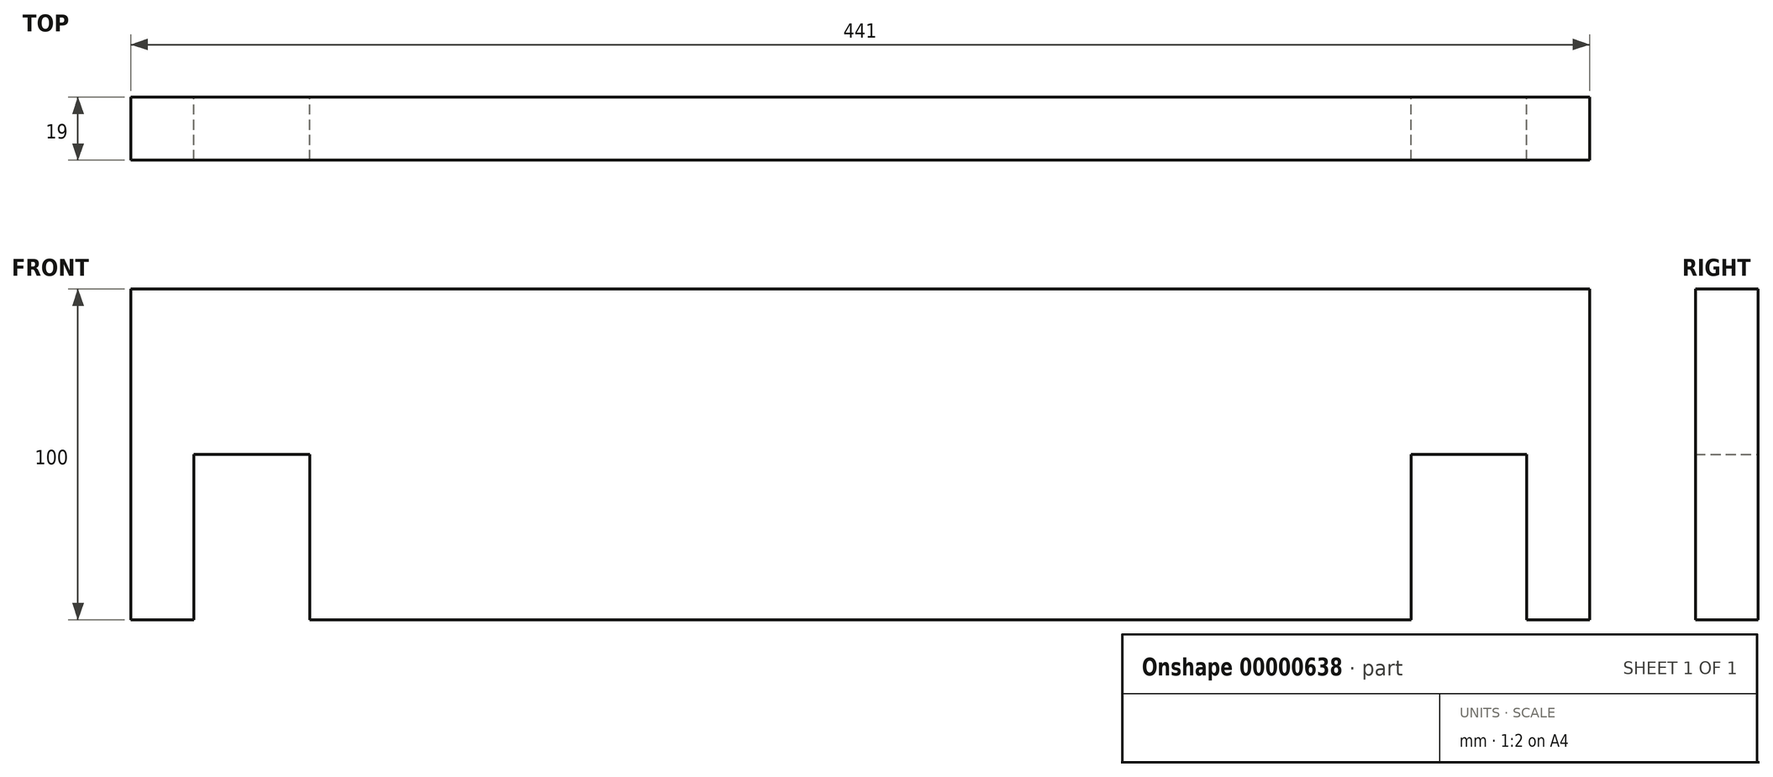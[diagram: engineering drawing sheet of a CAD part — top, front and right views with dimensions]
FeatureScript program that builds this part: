
annotation { "Feature Type Name" : "Feature", "Feature Type Description" : "" }
export const myFeature = defineFeature(function(context is Context, id is Id, definition is map)
    precondition{}
    {
        {
            var Q0;
            Q0=qCreatedBy(makeId("Front.planeOp"),FACE);
            var sketch = newSketch(context, id + "F0", { "sketchPlane" : qUnion([Q0])});
            skLineSegment(sketch, "E0.bottom", {"start": v(-220.5, 57.39) * mm, "end": v(220.5, 57.39) * mm});
            skLineSegment(sketch, "E0.top", {"start": v(-220.5, -42.61) * mm, "end": v(-201.5, -42.61) * mm});
            skLineSegment(sketch, "E0.left", {"start": v(-220.5, 57.39) * mm, "end": v(-220.5, -42.61) * mm});
            skLineSegment(sketch, "E0.right", {"start": v(220.5, 57.39) * mm, "end": v(220.5, -42.61) * mm});
            skLineSegment(sketch, "E1", {"start": v(0, -42.61) * mm, "end": v(0, 0) * mm, "construction": true});
            skLineSegment(sketch, "E2.top", {"start": v(-201.5, 7.39) * mm, "end": v(-166.5, 7.39) * mm});
            skLineSegment(sketch, "E2.left", {"start": v(-201.5, -42.61) * mm, "end": v(-201.5, 7.39) * mm});
            skLineSegment(sketch, "E2.right", {"start": v(-166.5, -42.61) * mm, "end": v(-166.5, 7.39) * mm});
            skLineSegment(sketch, "E3.top", {"start": v(166.5, 7.39) * mm, "end": v(201.5, 7.39) * mm});
            skLineSegment(sketch, "E3.left", {"start": v(166.5, -42.61) * mm, "end": v(166.5, 7.39) * mm});
            skLineSegment(sketch, "E3.right", {"start": v(201.5, -42.61) * mm, "end": v(201.5, 7.39) * mm});
            skLineSegment(sketch, "E4.trimOffspring", {"start": v(-166.5, -42.61) * mm, "end": v(166.5, -42.61) * mm});
            skLineSegment(sketch, "E5.trimOffspring", {"start": v(201.5, -42.61) * mm, "end": v(220.5, -42.61) * mm});
            skSolve(sketch);
        }
        {
            var Q0;
            Q0=makeQuery(id+"F0.imprint","IMPRINT",FACE,{"disambiguationData":[TD([[makeQuery(id+"F0.imprint","IMPRINT",EDGE,{"derivedFrom":sQuery(id+"F0.wireOp",EDGE,"E0.bottom")}),-1.0]])]});
            extrude(context, id + "F1", {"entities" : qUnion([Q0]), "depth" : 19 * mm});
        }
    });
